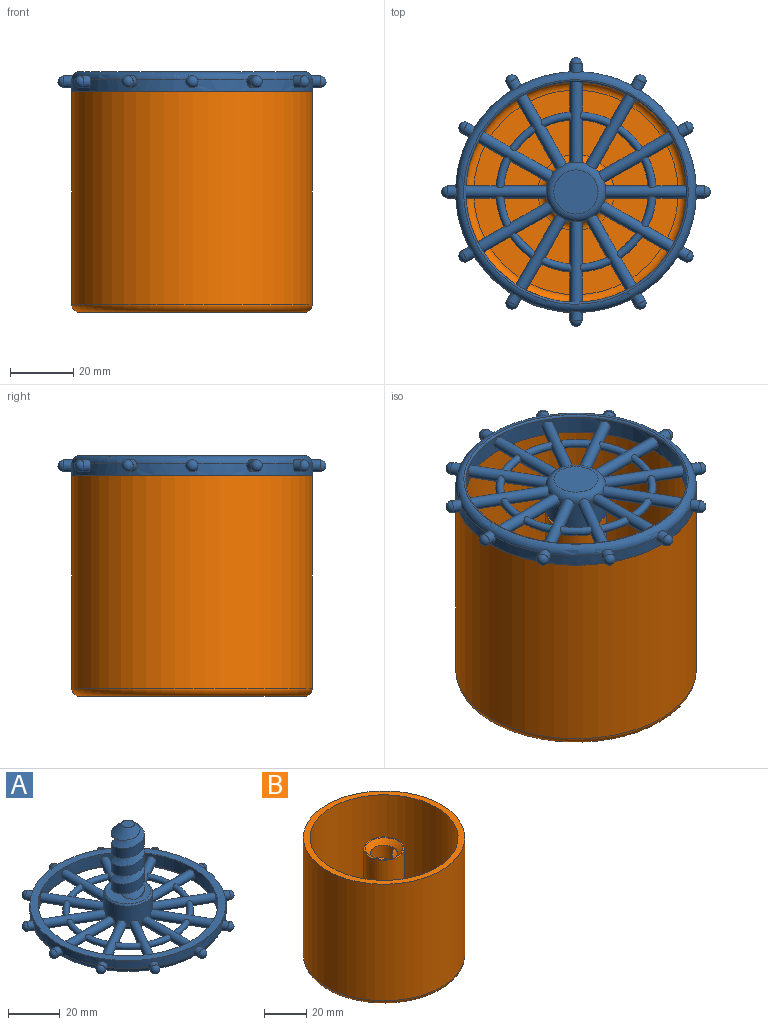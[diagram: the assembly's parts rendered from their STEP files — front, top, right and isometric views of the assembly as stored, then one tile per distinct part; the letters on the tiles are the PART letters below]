
ASSEMBLY  parts=2 mates=1
PART A: 73 faces, bbox 86.1x86.1x45.5 mm
  f0: cylinder r=1.91mm len=4.59mm, axis (-0.87,0.5,0), area 30.8mm2, adj f1,f3,f4
  f1: sphere r=1.91mm, area 22.8mm2, adj f0
  f2: cylinder r=34.92mm len=69.85mm, axis (0,0,1), area 1117.1mm2, adj f12,f13,f34,f35,f36,f37,f38,f39
  f3: cylinder r=38.1mm len=76.2mm, axis (0,0,1), area 815.1mm2, adj f0,f4,f9,f12,f15,f17,f19,f21
  f4: torus R=35.56mm, axis (0,0,1), area 891.8mm2, adj f0,f3,f9,f13,f15,f17,f19,f21
  f5: cylinder r=9.53mm len=19.05mm, axis (0,0,1), area 472.6mm2, adj f6,f34,f35,f36,f37,f38,f39,f40
  f6: torus R=6.99mm, axis (0,0,1), area 175.3mm2, adj f5,f34,f35,f36,f37,f38,f39,f40
  f7: torus R=24.13mm, axis (0,0,1), area 74.1mm2, adj f54,f55
  f8: torus R=24.13mm, axis (0,0,1), area 74.1mm2, adj f37,f55
  f9: cylinder r=1.91mm len=4.59mm, axis (-0.5,0.87,0), area 30.8mm2, adj f3,f4,f10
  f10: sphere r=1.91mm, area 22.8mm2, adj f9
  f11: torus R=24.13mm, axis (0,0,1), area 74.1mm2, adj f35,f54
  f12: plane 76.2x76.2mm, normal (0,0,1), area 728.4mm2, adj f2,f3
  f13: torus R=35.56mm, axis (0,0,1), area 220.3mm2, adj f2,f4
  f14: sphere r=1.91mm, area 22.8mm2, adj f15
  f15: cylinder r=1.91mm len=4.59mm, axis (-0.87,-0.5,0), area 30.8mm2, adj f3,f4,f14
  f16: sphere r=1.91mm, area 22.8mm2, adj f17
  f17: cylinder r=1.91mm len=4.59mm, axis (-0.5,-0.87,0), area 30.8mm2, adj f3,f4,f16
  f18: sphere r=1.91mm, area 22.8mm2, adj f19
  f19: cylinder r=1.91mm len=3.81mm, axis (0,-1,0), area 30.8mm2, adj f3,f4,f18
  f20: sphere r=1.91mm, area 22.8mm2, adj f21
  f21: cylinder r=1.91mm len=4.59mm, axis (0.5,-0.87,0), area 30.8mm2, adj f3,f4,f20
  f22: sphere r=1.91mm, area 22.8mm2, adj f23
  f23: cylinder r=1.91mm len=4.59mm, axis (0.87,-0.5,0), area 30.8mm2, adj f3,f4,f22
  f24: sphere r=1.91mm, area 22.8mm2, adj f25
  f25: cylinder r=1.91mm len=3.81mm, axis (1,0,0), area 30.8mm2, adj f3,f4,f24
  f26: sphere r=1.91mm, area 22.8mm2, adj f27
  f27: cylinder r=1.91mm len=3.81mm, axis (1,0,0), area 31.5mm2, adj f3,f4,f26
  f28: sphere r=1.91mm, area 22.8mm2, adj f29
  f29: cylinder r=1.91mm len=4.59mm, axis (0.5,0.87,0), area 30.8mm2, adj f3,f4,f28
  f30: sphere r=1.91mm, area 22.8mm2, adj f31
  f31: cylinder r=1.91mm len=3.81mm, axis (0,1,0), area 30.8mm2, adj f3,f4,f30
  f32: sphere r=1.91mm, area 22.8mm2, adj f33
  f33: cylinder r=1.91mm len=4.59mm, axis (0.87,0.5,0), area 30.8mm2, adj f3,f4,f32
  f34: cylinder r=1.91mm len=24.05mm, axis (0.87,0.5,0), area 294.6mm2, adj f2,f5,f6,f51,f52
  f35: cylinder r=1.91mm len=25.57mm, axis (0,1,0), area 294.6mm2, adj f2,f5,f6,f11,f53
  f36: cylinder r=1.91mm len=24.05mm, axis (0.5,0.87,0), area 294.6mm2, adj f2,f5,f6,f52,f53
  f37: cylinder r=1.91mm len=25.74mm, axis (1,0,0), area 295mm2, adj f2,f5,f6,f8,f46
  f38: cylinder r=1.91mm len=25.74mm, axis (1,0,0), area 294.9mm2, adj f2,f5,f6,f50,f51
  f39: cylinder r=1.91mm len=24.05mm, axis (0.87,-0.5,0), area 294.6mm2, adj f2,f5,f6,f49,f50
  f40: cylinder r=1.91mm len=24.05mm, axis (0.5,-0.87,0), area 294.6mm2, adj f2,f5,f6,f48,f49
  f41: cylinder r=1.91mm len=25.57mm, axis (0,-1,0), area 294.6mm2, adj f2,f5,f6,f47,f48
  f42: cylinder r=1.91mm len=24.05mm, axis (-0.5,-0.87,0), area 294.6mm2, adj f2,f5,f6,f45,f47
  f43: cylinder r=1.91mm len=24.05mm, axis (-0.87,-0.5,0), area 294.6mm2, adj f2,f5,f6,f45,f46
  f44: plane 13.97x13.97mm, normal (0,0,-1), area 153.3mm2, adj f6
  f45: torus R=24.13mm, axis (0,0,1), area 74.1mm2, adj f42,f43
  f46: torus R=24.13mm, axis (0,0,1), area 74.1mm2, adj f37,f43
  f47: torus R=24.13mm, axis (0,0,1), area 74.1mm2, adj f41,f42
  f48: torus R=24.13mm, axis (0,0,1), area 74.1mm2, adj f40,f41
  f49: torus R=24.13mm, axis (0,0,1), area 74.1mm2, adj f39,f40
  f50: torus R=24.13mm, axis (0,0,1), area 74.1mm2, adj f38,f39
  f51: torus R=24.13mm, axis (0,0,1), area 74.1mm2, adj f34,f38
  f52: torus R=24.13mm, axis (0,0,1), area 74.1mm2, adj f34,f36
  f53: torus R=24.13mm, axis (0,0,1), area 74.2mm2, adj f35,f36
  f54: cylinder r=1.91mm len=24.05mm, axis (-0.5,0.87,0), area 294.6mm2, adj f2,f5,f6,f7,f11
  f55: cylinder r=1.91mm len=24.05mm, axis (-0.87,0.5,0), area 294.6mm2, adj f2,f5,f6,f7,f8
  f56: plane 18.83x18.83mm, normal (0,0,1), area 146.1mm2, adj f60,f61,f62,f63
  f57: plane 5.08x5.08mm, normal (0,0,1), area 20.3mm2, adj f59
  f58: plane 3.3x2.42mm, normal (0,-1,0), area 1.7mm2, adj f59,f61,f62
  f59: cone r=2.54mm half-angle=45deg, axis (0,0,-1), area 123.7mm2, adj f57,f58,f60,f62
  f60: cylinder r=6.35mm len=27.94mm, axis (0,0,-1), area 614.2mm2, adj f56,f59,f61,f62
  f61: bspline ~31.75x12.7mm, area 395mm2, adj f56,f58,f60,f62
  f62: bspline ~33.66x12.7mm, area 401.4mm2, adj f56,f58,f59,f60,f61
  f63: cone r=8.89mm half-angle=45deg, axis (0,0,-1), area 52mm2, adj f5,f56
  f64: plane 12.39x6.35mm, normal (0,0,-1), area 24.5mm2, adj f70,f71,f72
  f65: cylinder r=1.91mm len=3.24mm, axis (1,0,0), area 4.1mm2, adj f66,f69,f71,f72
  f66: plane 2.2x1.27mm, normal (0,-1,0), area 1.4mm2, adj f65,f71,f72
  f67: cylinder r=1.91mm len=2.42mm, axis (0,1,0), area 1.3mm2, adj f70,f72
  f68: cylinder r=1.91mm len=3.69mm, axis (0.5,0.87,0), area 3.5mm2, adj f69,f70,f72
  f69: cylinder r=1.91mm len=4.39mm, axis (0.87,0.5,0), area 7.9mm2, adj f65,f68,f70,f71,f72
  f70: bspline ~12.7x6.35mm, area 19.6mm2, adj f64,f67,f68,f69,f71,f72
  f71: bspline ~10.84x6.35mm, area 10.9mm2, adj f64,f65,f66,f69,f70
  f72: cylinder r=6.35mm len=12.39mm, axis (0,0,-1), area 21.9mm2, adj f64,f65,f66,f67,f68,f69,f70
PART B: 22 faces, bbox 83.1x83.1x70.4 mm
  f0: bspline ~37.38x12.7mm, area 378.4mm2, adj f1,f10,f11,f12,f13,f14,f16,f21
  f1: bspline ~36.32x12.7mm, area 359.3mm2, adj f0,f9,f11,f12,f13,f14,f16,f21
  f2: cylinder r=38.1mm len=76.2mm, axis (0,0,1), area 16113.3mm2, adj f4,f20
  f3: plane 71.12x71.12mm, normal (0,0,-1), area 3724.3mm2, adj f17,f20
  f4: plane 76.2x76.2mm, normal (0,0,1), area 728.4mm2, adj f2,f5
  f5: cylinder r=34.92mm len=69.85mm, axis (0,0,1), area 14213.1mm2, adj f4,f19
  f6: plane 64.77x64.77mm, normal (0,0,1), area 2837.6mm2, adj f18,f19
  f7: cylinder r=9.53mm len=58.42mm, axis (0,0,-1), area 3496.3mm2, adj f8,f18
  f8: plane 19.05x19.05mm, normal (0,0,1), area 36.7mm2, adj f7,f15
  f9: cylinder r=6.35mm len=28.53mm, axis (0,0,-1), area 987.9mm2, adj f1,f14,f16,f17
  f10: cylinder r=6.35mm len=6.03mm, axis (0,0,-1), area 6.7mm2, adj f0,f11,f15
  f11: cylinder r=6.35mm len=12.7mm, axis (0,0,-1), area 210.3mm2, adj f0,f1,f10,f12,f15,f21
  f12: cylinder r=6.35mm len=14.14mm, axis (0,0,-1), area 226.3mm2, adj f0,f1,f11,f13
  f13: cylinder r=6.35mm len=14.14mm, axis (0,0,-1), area 226.3mm2, adj f0,f1,f12,f14
  f14: cylinder r=6.35mm len=14.14mm, axis (0,0,-1), area 226.3mm2, adj f0,f1,f9,f13
  f15: cone r=6.35mm half-angle=45deg, axis (0,0,1), area 172mm2, adj f8,f10,f11
  f16: plane 11.26x4.96mm, normal (0,0,-1), area 13.9mm2, adj f0,f1,f9
  f17: torus R=8.89mm, axis (0,0,1), area 182.3mm2, adj f3,f9
  f18: torus R=12.06mm, axis (0,0,1), area 261.9mm2, adj f6,f7
  f19: torus R=32.38mm, axis (0,0,1), area 852.4mm2, adj f5,f6
  f20: torus R=35.56mm, axis (0,0,1), area 932mm2, adj f2,f3
  f21: bspline ~4.01x3.77mm, area 5.2mm2, adj f0,f1,f11
PLACE A rot(axis=(1,0,0),180deg) t=(-73.62,-29.32,82.29)mm
PLACE B rot(axis=(0,0,-1),54deg) t=(-73.62,-29.32,12.44)mm
MATE cylindrical A.f59 <-> B.f9  axis (0,0,-1) through (-73.62,-29.32,44.19)mm
